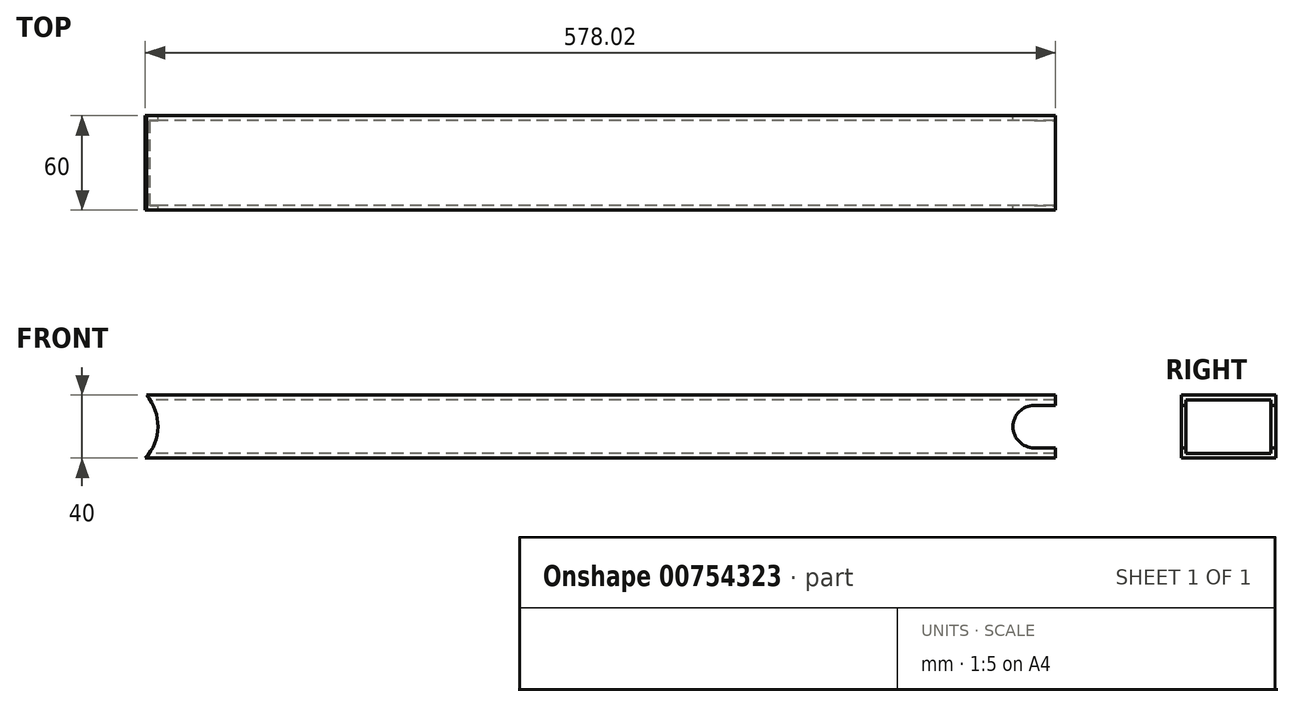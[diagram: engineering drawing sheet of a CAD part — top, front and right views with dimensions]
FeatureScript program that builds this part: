
annotation { "Feature Type Name" : "Feature", "Feature Type Description" : "" }
export const myFeature = defineFeature(function(context is Context, id is Id, definition is map)
    precondition{}
    {
        {
            var Q0;
            Q0=qCreatedBy(makeId("Right.planeOp"),FACE);
            var sketch = newSketch(context, id + "F0", { "sketchPlane" : qUnion([Q0])});
            skLineSegment(sketch, "E0.bottom", {"start": v(0, 19.59) * mm, "end": v(-60, 19.59) * mm});
            skLineSegment(sketch, "E0.top", {"start": v(0, -20.41) * mm, "end": v(-60, -20.41) * mm});
            skLineSegment(sketch, "E0.left", {"start": v(0, 19.59) * mm, "end": v(0, -20.41) * mm});
            skLineSegment(sketch, "E0.right", {"start": v(-60, 19.59) * mm, "end": v(-60, -20.41) * mm});
            skLineSegment(sketch, "E1.bottom", {"start": v(-3, 16.59) * mm, "end": v(-57, 16.59) * mm});
            skLineSegment(sketch, "E1.top", {"start": v(-3, -17.41) * mm, "end": v(-57, -17.41) * mm});
            skLineSegment(sketch, "E1.left", {"start": v(-3, 16.59) * mm, "end": v(-3, -17.41) * mm});
            skLineSegment(sketch, "E1.right", {"start": v(-57, 16.59) * mm, "end": v(-57, -17.41) * mm});
            skLineSegment(sketch, "E2", {"start": v(-51.52, -17.41) * mm, "end": v(-51.52, -20.41) * mm, "construction": true});
            skLineSegment(sketch, "E3", {"start": v(-57, -11.2) * mm, "end": v(-60, -11.2) * mm, "construction": true});
            skSolve(sketch);
        }
        {
            var Q0;
            Q0=makeQuery(id+"F0.imprint","IMPRINT",FACE,{"disambiguationData":[TD([[makeQuery(id+"F0.imprint","IMPRINT",EDGE,{"derivedFrom":sQuery(id+"F0.wireOp",EDGE,"E0.bottom")}),1.0]])]});
            extrude(context, id + "F1", {"entities" : qUnion([Q0]), "depth" : 600 * mm, "offsetDistance" : 25 * mm});
        }
        {
            var Q0;
            Q0=makeQuery(id+"F1.opExtrude","SWEPT_FACE",FACE,{"disambiguationData":[OSD([sQuery(id+"F0.wireOp",EDGE,"E0.left")])]});
            var sketch = newSketch(context, id + "F2", { "sketchPlane" : qUnion([Q0])});
            skLineSegment(sketch, "E4", {"start": v(-586.55, 19.59) * mm, "end": v(-586.55, -20.41) * mm, "construction": true});
            skLineSegment(sketch, "E5", {"start": v(-586.55, 19.59) * mm, "end": v(-600, 19.59) * mm, "construction": true});
            skCircle(sketch, "E6", {"center": v(-586.55, -0.41) * mm, "radius": 13.45 * mm});
            skLineSegment(sketch, "E7", {"start": v(-586.55, 19.59) * mm, "end": v(-586.55, 13.04) * mm, "construction": true});
            skLineSegment(sketch, "E8", {"start": v(-586.55, -20.41) * mm, "end": v(-586.55, -13.86) * mm, "construction": true});
            skLineSegment(sketch, "E9", {"start": v(-600, -13.86) * mm, "end": v(-586.55, -13.86) * mm});
            skLineSegment(sketch, "E10", {"start": v(-586.55, 13.04) * mm, "end": v(-600, 13.04) * mm});
            skCircle(sketch, "E11", {"center": v(0, 0) * mm, "radius": 30 * mm});
            skSolve(sketch);
        }
        {
            var Q0;
            Q0 = qSketchRegion(id + "F2", true);
            var Q1;
            {var subQ0=sQuery(id+"F2.wireOp",EDGE,"E10");Q1=makeQuery(id+"F2.imprint","IMPRINT",FACE,{"disambiguationData":[TD([[makeQuery(id+"F2.imprint","IMPRINT",EDGE,{"derivedFrom":subQ0}),1.0]])]});}
            var Q2;
            {var subQ0=sQuery(id+"F2.wireOp",EDGE,"E9");Q2=makeQuery(id+"F2.imprint","IMPRINT",FACE,{"disambiguationData":[TD([[makeQuery(id+"F2.imprint","IMPRINT",EDGE,{"derivedFrom":subQ0}),1.0]])]});}
            extrude(context, id + "F3", {"entities" : qUnion([Q0, Q1, Q2]), "operationType" : NewBodyOperationType.REMOVE, "oppositeDirection" : true, "depth" : 60 * mm, "offsetDistance" : 25 * mm});
        }
        {
            var Q0;
            Q0 = qSketchRegion(id + "F2", true);
            extrude(context, id + "F4", {"entities" : qUnion([Q0]), "operationType" : NewBodyOperationType.REMOVE, "oppositeDirection" : true, "depth" : 25 * mm, "offsetDistance" : 25 * mm});
        }
    });
